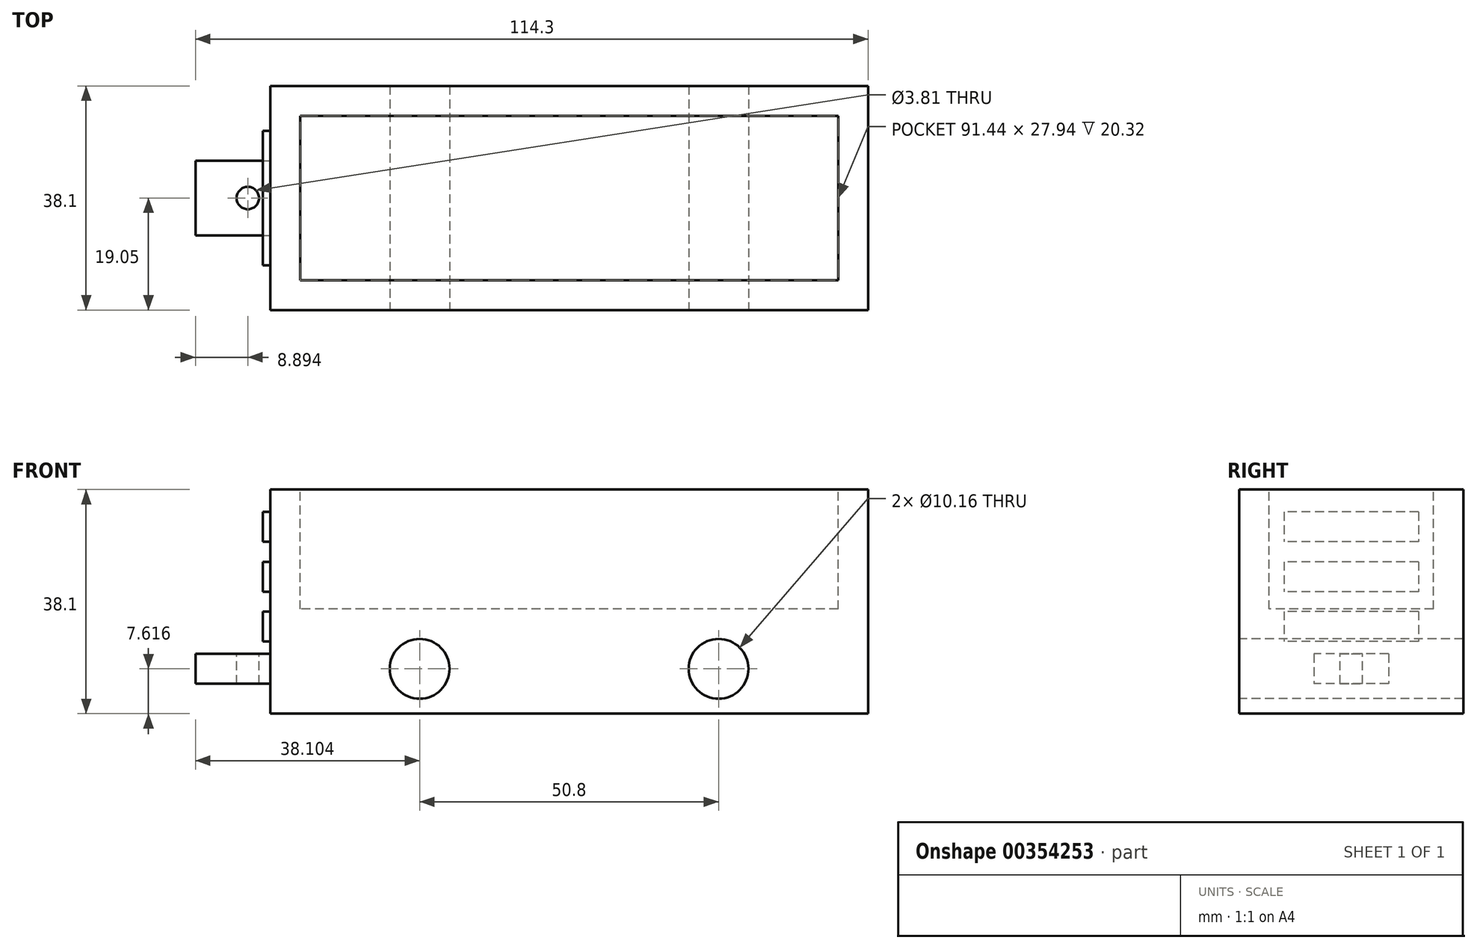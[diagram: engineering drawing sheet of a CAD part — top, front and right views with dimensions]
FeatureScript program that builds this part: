
annotation { "Feature Type Name" : "Feature", "Feature Type Description" : "" }
export const myFeature = defineFeature(function(context is Context, id is Id, definition is map)
    precondition{}
    {
        {
            var Q0;
            Q0=qCreatedBy(makeId("Front.planeOp"),FACE);
            var sketch = newSketch(context, id + "F0", { "sketchPlane" : qUnion([Q0])});
            skLineSegment(sketch, "E0.bottom", {"start": v(-53.18, 18.59) * mm, "end": v(48.42, 18.59) * mm});
            skLineSegment(sketch, "E0.top", {"start": v(-53.18, -19.51) * mm, "end": v(48.42, -19.51) * mm});
            skLineSegment(sketch, "E0.left", {"start": v(-53.18, 18.59) * mm, "end": v(-53.18, -19.51) * mm});
            skLineSegment(sketch, "E0.right", {"start": v(48.42, 18.59) * mm, "end": v(48.42, -19.51) * mm});
            skSolve(sketch);
        }
        {
            var Q0;
            Q0 = qSketchRegion(id + "F0", true);
            extrude(context, id + "F1", {"entities" : qUnion([Q0]), "depth" : 38.1 * mm});
        }
        {
            var Q0;
            Q0=makeQuery(id+"F1.opExtrude","SWEPT_FACE",FACE,{"disambiguationData":[OSD([sQuery(id+"F0.wireOp",EDGE,"E0.bottom")])]});
            var sketch = newSketch(context, id + "F2", { "sketchPlane" : qUnion([Q0])});
            skLineSegment(sketch, "E1.bottom", {"start": v(43.34, -5.08) * mm, "end": v(-48.1, -5.08) * mm});
            skLineSegment(sketch, "E1.top", {"start": v(43.34, -33.02) * mm, "end": v(-48.1, -33.02) * mm});
            skLineSegment(sketch, "E1.left", {"start": v(43.34, -5.08) * mm, "end": v(43.34, -33.02) * mm});
            skLineSegment(sketch, "E1.right", {"start": v(-48.1, -5.08) * mm, "end": v(-48.1, -33.02) * mm});
            skSolve(sketch);
        }
        {
            var Q0;
            Q0=makeQuery(id+"F2.imprint","IMPRINT",FACE,{"disambiguationData":[TD([[makeQuery(id+"F2.imprint","IMPRINT",EDGE,{"derivedFrom":sQuery(id+"F2.wireOp",EDGE,"E1.bottom")}),1.0]])]});
            extrude(context, id + "F3", {"entities" : qUnion([Q0]), "operationType" : NewBodyOperationType.REMOVE, "oppositeDirection" : true, "depth" : 20.32 * mm});
        }
        {
            var Q0;
            Q0=makeQuery(id+"F1.opExtrude","CAP_FACE",FACE,{"disambiguationData":[OSD([sQuery(id+"F0.wireOp",EDGE,"E0.bottom"),sQuery(id+"F0.wireOp",EDGE,"E0.top"),sQuery(id+"F0.wireOp",EDGE,"E0.left"),sQuery(id+"F0.wireOp",EDGE,"E0.right")])],"isStart":false});
            var sketch = newSketch(context, id + "F4", { "sketchPlane" : qUnion([Q0])});
            skCircle(sketch, "E2", {"center": v(-27.78, -11.9) * mm, "radius": 5.08 * mm});
            skCircle(sketch, "E3", {"center": v(23.02, -11.9) * mm, "radius": 5.08 * mm});
            skSolve(sketch);
        }
        {
            var Q0;
            Q0=makeQuery(id+"F4.imprint","IMPRINT",FACE,{"disambiguationData":[TD([[makeQuery(id+"F4.imprint","IMPRINT",EDGE,{"derivedFrom":sQuery(id+"F4.wireOp",EDGE,"E2")}),1.0]])]});
            var Q1;
            Q1=makeQuery(id+"F4.imprint","IMPRINT",FACE,{"disambiguationData":[TD([[makeQuery(id+"F4.imprint","IMPRINT",EDGE,{"derivedFrom":sQuery(id+"F4.wireOp",EDGE,"E3")}),1.0]])]});
            extrude(context, id + "F5", {"entities" : qUnion([Q0, Q1]), "operationType" : NewBodyOperationType.REMOVE, "endBound" : BoundingType.THROUGH_ALL, "oppositeDirection" : true, "depth" : 25.4 * mm});
        }
        {
            var Q0;
            Q0=makeQuery(id+"F1.opExtrude","SWEPT_FACE",FACE,{"disambiguationData":[OSD([sQuery(id+"F0.wireOp",EDGE,"E0.left")])]});
            var sketch = newSketch(context, id + "F6", { "sketchPlane" : qUnion([Q0])});
            skLineSegment(sketch, "E4.bottom", {"start": v(7.62, 14.78) * mm, "end": v(30.48, 14.78) * mm});
            skLineSegment(sketch, "E4.top", {"start": v(7.62, -15.7) * mm, "end": v(30.48, -15.7) * mm});
            skLineSegment(sketch, "E4.left", {"start": v(7.62, 14.78) * mm, "end": v(7.62, -15.7) * mm});
            skLineSegment(sketch, "E4.right", {"start": v(30.48, 14.78) * mm, "end": v(30.48, -15.7) * mm});
            skLineSegment(sketch, "E5", {"start": v(7.62, 9.7) * mm, "end": v(30.48, 9.7) * mm});
            skLineSegment(sketch, "E6", {"start": v(7.62, 6.3) * mm, "end": v(30.48, 6.3) * mm});
            skLineSegment(sketch, "E7", {"start": v(7.62, 1.23) * mm, "end": v(30.48, 1.23) * mm});
            skLineSegment(sketch, "E8", {"start": v(7.62, -2.15) * mm, "end": v(30.48, -2.15) * mm});
            skLineSegment(sketch, "E9", {"start": v(7.62, -7.23) * mm, "end": v(30.48, -7.23) * mm});
            skLineSegment(sketch, "E10", {"start": v(7.62, -10.6) * mm, "end": v(30.48, -10.6) * mm});
            skSolve(sketch);
        }
        {
            var Q0;
            {var subQ0=sQuery(id+"F6.wireOp",EDGE,"E4.bottom");Q0=makeQuery(id+"F6.imprint","IMPRINT",FACE,{"disambiguationData":[TD([[makeQuery(id+"F6.imprint","IMPRINT",EDGE,{"derivedFrom":subQ0}),-1.0]])]});}
            var Q1;
            {var subQ0=sQuery(id+"F6.wireOp",EDGE,"E6");Q1=makeQuery(id+"F6.imprint","IMPRINT",FACE,{"disambiguationData":[TD([[makeQuery(id+"F6.imprint","IMPRINT",EDGE,{"derivedFrom":subQ0}),-1.0]])]});}
            var Q2;
            {var subQ0=sQuery(id+"F6.wireOp",EDGE,"E8");Q2=makeQuery(id+"F6.imprint","IMPRINT",FACE,{"disambiguationData":[TD([[makeQuery(id+"F6.imprint","IMPRINT",EDGE,{"derivedFrom":subQ0}),-1.0]])]});}
            extrude(context, id + "F7", {"entities" : qUnion([Q0, Q1, Q2]), "operationType" : NewBodyOperationType.ADD, "depth" : 1.27 * mm});
        }
        {
            var Q0;
            Q0=makeQuery(id+"F1.opExtrude","SWEPT_FACE",FACE,{"disambiguationData":[OSD([sQuery(id+"F0.wireOp",EDGE,"E0.left")])]});
            var sketch = newSketch(context, id + "F8", { "sketchPlane" : qUnion([Q0])});
            skLineSegment(sketch, "E11.bottom", {"start": v(12.7, -9.35) * mm, "end": v(25.4, -9.35) * mm});
            skLineSegment(sketch, "E11.top", {"start": v(12.7, -14.43) * mm, "end": v(25.4, -14.43) * mm});
            skLineSegment(sketch, "E11.left", {"start": v(12.7, -9.35) * mm, "end": v(12.7, -14.43) * mm});
            skLineSegment(sketch, "E11.right", {"start": v(25.4, -9.35) * mm, "end": v(25.4, -14.43) * mm});
            skSolve(sketch);
        }
        {
            var Q0;
            Q0 = qSketchRegion(id + "F8", true);
            extrude(context, id + "F9", {"entities" : qUnion([Q0]), "operationType" : NewBodyOperationType.ADD, "depth" : 12.7 * mm});
        }
        {
            var Q0;
            Q0=makeQuery(id+"F9.opExtrude","SWEPT_FACE",FACE,{"disambiguationData":[OSD([sQuery(id+"F8.wireOp",EDGE,"E11.bottom")])]});
            var sketch = newSketch(context, id + "F10", { "sketchPlane" : qUnion([Q0])});
            skCircle(sketch, "E12", {"center": v(-56.99, -19.05) * mm, "radius": 1.9 * mm});
            skSolve(sketch);
        }
        {
            var Q0;
            Q0=makeQuery(id+"F10.imprint","IMPRINT",FACE,{"disambiguationData":[TD([[makeQuery(id+"F10.imprint","IMPRINT",EDGE,{"derivedFrom":sQuery(id+"F10.wireOp",EDGE,"E12")}),1.0]])]});
            extrude(context, id + "F11", {"entities" : qUnion([Q0]), "operationType" : NewBodyOperationType.REMOVE, "endBound" : BoundingType.THROUGH_ALL, "oppositeDirection" : true, "depth" : 25.4 * mm});
        }
    });
